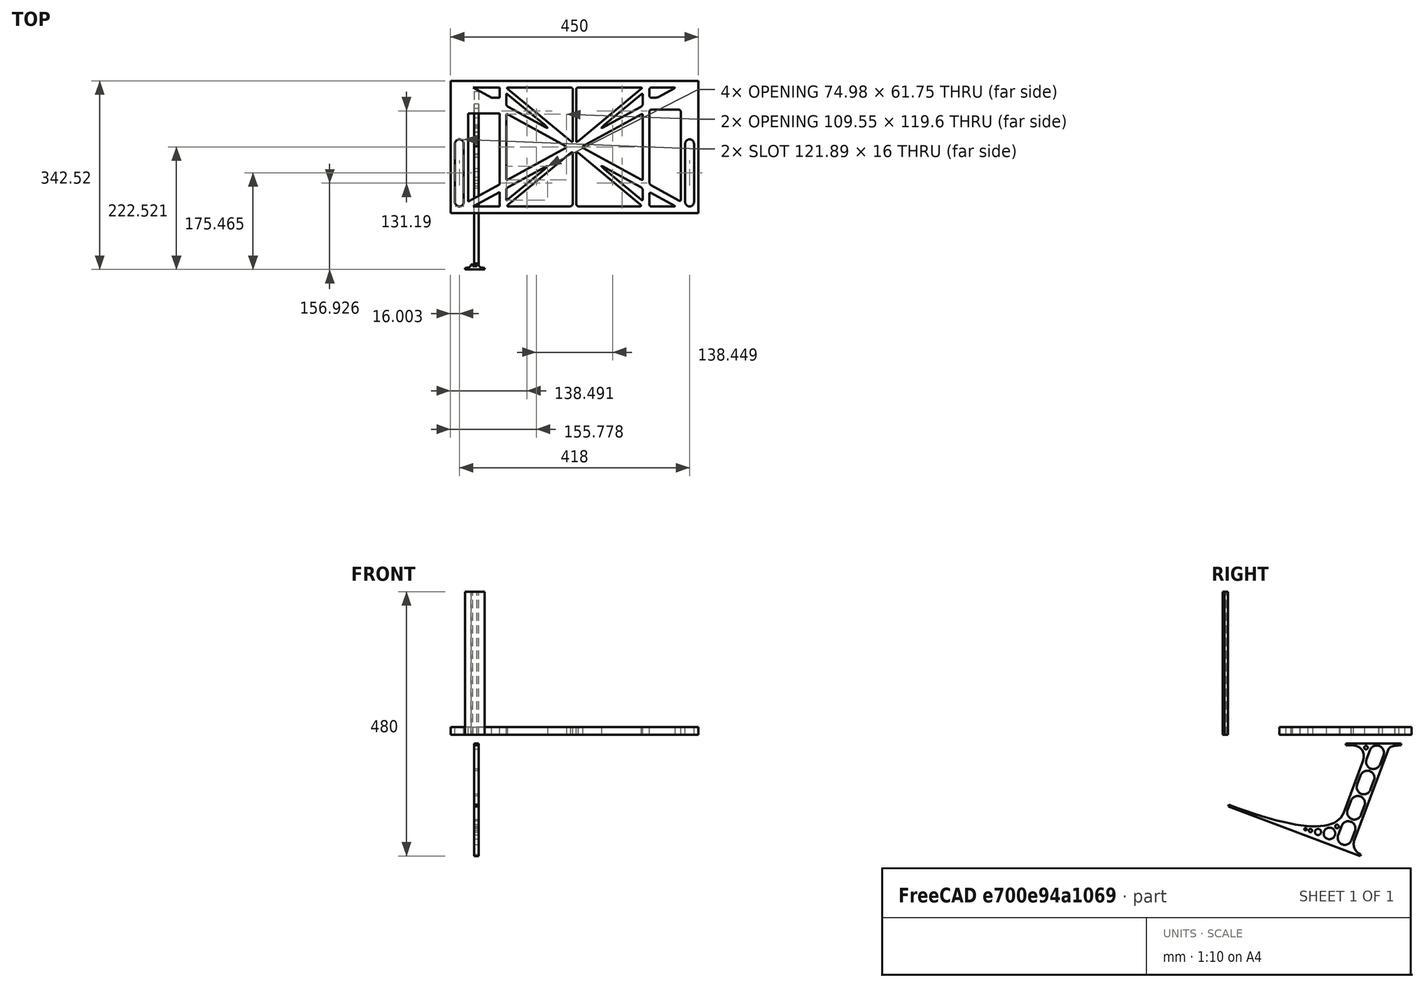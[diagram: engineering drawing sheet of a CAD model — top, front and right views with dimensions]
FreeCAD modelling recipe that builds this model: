
FCSTD DOCUMENT  (FreeCAD 0.19R0.19.2)
Label: laptopStand1145FCStd
License: All rights reserved
LicenseURL: http://en.wikipedia.org/wiki/All_rights_reserved
objects: Sketcher::SketchObject×3, Part::Extrusion×3
note: 6 computed .brp shape members not serialized (recipe doc carries the construction recipe); baked Part::Feature solids carry a one-line shape summary decoded from their .brp

FEATURE [Sketcher::SketchObject] Sketch
  FullyConstrained = false
  sketch-geometry (318):
    g0: LineSegment StartX=-10.9272 StartY=-82.7794 StartZ=0 EndX=46.0728 EndY=-51.4823 EndZ=0
    g1: LineSegment StartX=-10.9272 StartY=77.3346 StartZ=0 EndX=-10.9272 EndY=-82.7794 EndZ=0
    g2: LineSegment StartX=-1.92719 StartY=-91.7794 StartZ=0 EndX=46.0728 EndY=-91.7794 EndZ=0
    g3: LineSegment StartX=46.0728 StartY=-65.424 StartZ=0 EndX=-1.92719 EndY=-91.7794 EndZ=0
    g4: LineSegment StartX=46.0728 StartY=-65.424 StartZ=0 EndX=46.0728 EndY=-91.7794 EndZ=0
    g5: LineSegment StartX=46.0728 StartY=77.3346 StartZ=0 EndX=46.0728 EndY=-51.4823 EndZ=0
    g6: LineSegment StartX=-42.9272 StartY=136.221 StartZ=0 EndX=-42.9272 EndY=-103.779 EndZ=0
    g7: LineSegment StartX=407.073 StartY=136.221 StartZ=0 EndX=407.073 EndY=-103.779 EndZ=0
    g8: ArcOfCircle CenterX=-26.9272 CenterY=22.1087 CenterZ=0 NormalX=0 NormalY=0 NormalZ=1 AngleXU=0 Radius=8 StartAngle=1e-16 EndAngle=3.14159
    g9: ArcOfCircle CenterX=-26.9272 CenterY=-83.7794 CenterZ=0 NormalX=0 NormalY=0 NormalZ=1 AngleXU=0 Radius=8 StartAngle=3.14159 EndAngle=6.28319
    g10: LineSegment StartX=-34.9272 StartY=22.1087 StartZ=0 EndX=-34.9272 EndY=-83.7794 EndZ=0
    g11: LineSegment StartX=-18.9272 StartY=22.1087 StartZ=0 EndX=-18.9272 EndY=-83.7794 EndZ=0
    g12: ArcOfCircle CenterX=391.073 CenterY=22.1087 CenterZ=0 NormalX=0 NormalY=0 NormalZ=1 AngleXU=0 Radius=8 StartAngle=-4.4e-15 EndAngle=3.14159
    g13: LineSegment StartX=399.073 StartY=22.1087 StartZ=0 EndX=399.073 EndY=-83.7794 EndZ=0
    g14: LineSegment StartX=383.073 StartY=22.1087 StartZ=0 EndX=383.073 EndY=-83.7794 EndZ=0
    g15: ArcOfCircle CenterX=391.073 CenterY=-83.7794 CenterZ=0 NormalX=0 NormalY=0 NormalZ=1 AngleXU=0 Radius=8 StartAngle=3.14159 EndAngle=6.28319
    g16: Circle CenterX=175.022 CenterY=27.0628 CenterZ=0 NormalX=0 NormalY=0 NormalZ=1 AngleXU=0 Radius=1
    g17: Circle CenterX=179.022 CenterY=24.8665 CenterZ=0 NormalX=0 NormalY=0 NormalZ=1 AngleXU=0 Radius=1
    g18: Circle CenterX=179.022 CenterY=27.0628 CenterZ=0 NormalX=0 NormalY=0 NormalZ=1 AngleXU=0 Radius=1
    g19: BSplineCurve PolesCount=3 KnotsCount=2 Degree=2 IsPeriodic=0
    g20: GeomPoint X=175.022 Y=27.0628 Z=0
    g21: GeomPoint X=179.022 Y=27.0628 Z=0
    g22: Circle CenterX=189.124 CenterY=27.0628 CenterZ=0 NormalX=0 NormalY=0 NormalZ=1 AngleXU=0 Radius=1
    g23: Circle CenterX=185.124 CenterY=24.8665 CenterZ=0 NormalX=0 NormalY=0 NormalZ=1 AngleXU=0 Radius=1
    g24: Circle CenterX=185.124 CenterY=27.0628 CenterZ=0 NormalX=0 NormalY=0 NormalZ=1 AngleXU=0 Radius=1
    g25: BSplineCurve PolesCount=3 KnotsCount=2 Degree=2 IsPeriodic=0
    g26: GeomPoint X=189.124 Y=27.0628 Z=0
    g27: GeomPoint X=185.124 Y=27.0628 Z=0
    g28: Circle CenterX=175.022 CenterY=5.37834 CenterZ=0 NormalX=0 NormalY=0 NormalZ=1 AngleXU=0 Radius=1
    g29: Circle CenterX=179.022 CenterY=7.57463 CenterZ=0 NormalX=0 NormalY=0 NormalZ=1 AngleXU=0 Radius=1
    g30: Circle CenterX=179.022 CenterY=5.34704 CenterZ=0 NormalX=0 NormalY=0 NormalZ=1 AngleXU=0 Radius=1
    g31: BSplineCurve PolesCount=3 KnotsCount=2 Degree=2 IsPeriodic=0
    g32: GeomPoint X=175.022 Y=5.37834 Z=0
    g33: GeomPoint X=179.022 Y=5.34704 Z=0
    g34: Circle CenterX=189.124 CenterY=5.37834 CenterZ=0 NormalX=0 NormalY=0 NormalZ=1 AngleXU=0 Radius=1
    g35: Circle CenterX=185.124 CenterY=7.57463 CenterZ=0 NormalX=0 NormalY=0 NormalZ=1 AngleXU=0 Radius=1
    g36: Circle CenterX=185.124 CenterY=5.34704 CenterZ=0 NormalX=0 NormalY=0 NormalZ=1 AngleXU=0 Radius=1
    g37: BSplineCurve PolesCount=3 KnotsCount=2 Degree=2 IsPeriodic=0
    g38: GeomPoint X=189.124 Y=5.37834 Z=0
    g39: GeomPoint X=185.124 Y=5.34704 Z=0
    g40: Circle CenterX=165.871 CenterY=18.1458 CenterZ=0 NormalX=0 NormalY=0 NormalZ=1 AngleXU=0 Radius=1
    g41: Circle CenterX=169.377 CenterY=16.2206 CenterZ=0 NormalX=0 NormalY=0 NormalZ=1 AngleXU=0 Radius=1
    g42: Circle CenterX=165.871 CenterY=14.2954 CenterZ=0 NormalX=0 NormalY=0 NormalZ=1 AngleXU=0 Radius=1
    g43: BSplineCurve PolesCount=3 KnotsCount=2 Degree=2 IsPeriodic=0
    g44: GeomPoint X=165.871 Y=18.1458 Z=0
    g45: GeomPoint X=165.871 Y=14.2954 Z=0
    g46: Circle CenterX=198.275 CenterY=18.1458 CenterZ=0 NormalX=0 NormalY=0 NormalZ=1 AngleXU=0 Radius=1
    g47: Circle CenterX=194.768 CenterY=16.2206 CenterZ=0 NormalX=0 NormalY=0 NormalZ=1 AngleXU=0 Radius=1
    g48: Circle CenterX=198.275 CenterY=14.2954 CenterZ=0 NormalX=0 NormalY=0 NormalZ=1 AngleXU=0 Radius=1
    g49: BSplineCurve PolesCount=3 KnotsCount=2 Degree=2 IsPeriodic=0
    g50: GeomPoint X=198.275 Y=18.1458 Z=0
    g51: GeomPoint X=198.275 Y=14.2954 Z=0
    g52: LineSegment StartX=407.073 StartY=-103.779 StartZ=0 EndX=-42.9272 EndY=-103.779 EndZ=0
    g53: LineSegment StartX=407.073 StartY=136.221 StartZ=0 EndX=-42.9272 EndY=136.221 EndZ=0
    g54: LineSegment StartX=46.0728 StartY=77.3346 StartZ=0 EndX=-10.9272 EndY=77.3346 EndZ=0
    g55: LineSegment StartX=46.0728 StartY=105.865 StartZ=0 EndX=31.5028 EndY=105.865 EndZ=0
    g56: LineSegment StartX=46.0728 StartY=124.221 StartZ=0 EndX=46.0728 EndY=105.865 EndZ=0
    g57: LineSegment StartX=-1.92719 StartY=124.221 StartZ=0 EndX=31.5028 EndY=105.865 EndZ=0
    g58: LineSegment StartX=46.0728 StartY=124.221 StartZ=0 EndX=-1.92719 EndY=124.221 EndZ=0
    g59: Circle CenterX=125.607 CenterY=54.1951 CenterZ=0 NormalX=0 NormalY=0 NormalZ=1 AngleXU=0 Radius=1
    g60: Circle CenterX=139.632 CenterY=46.4944 CenterZ=0 NormalX=0 NormalY=0 NormalZ=1 AngleXU=0 Radius=1
    g61: Circle CenterX=127.326 CenterY=56.7187 CenterZ=0 NormalX=0 NormalY=0 NormalZ=1 AngleXU=0 Radius=1
    g62: BSplineCurve PolesCount=3 KnotsCount=2 Degree=2 IsPeriodic=0
    g63: GeomPoint X=125.607 Y=54.1951 Z=0
    g64: GeomPoint X=127.326 Y=56.7187 Z=0
    g65: Circle CenterX=236.821 CenterY=56.7187 CenterZ=0 NormalX=0 NormalY=0 NormalZ=1 AngleXU=0 Radius=1
    g66: Circle CenterX=224.513 CenterY=46.4944 CenterZ=0 NormalX=0 NormalY=0 NormalZ=1 AngleXU=0 Radius=1
    g67: Circle CenterX=238.538 CenterY=54.1951 CenterZ=0 NormalX=0 NormalY=0 NormalZ=1 AngleXU=0 Radius=1
    g68: BSplineCurve PolesCount=3 KnotsCount=2 Degree=2 IsPeriodic=0
    g69: GeomPoint X=236.821 Y=56.7187 Z=0
    g70: GeomPoint X=238.538 Y=54.1951 Z=0
    g71: Circle CenterX=238.538 CenterY=-21.7539 CenterZ=0 NormalX=0 NormalY=0 NormalZ=1 AngleXU=0 Radius=1
    g72: Circle CenterX=224.513 CenterY=-14.0532 CenterZ=0 NormalX=0 NormalY=0 NormalZ=1 AngleXU=0 Radius=1
    g73: Circle CenterX=236.821 CenterY=-24.2775 CenterZ=0 NormalX=0 NormalY=0 NormalZ=1 AngleXU=0 Radius=1
    g74: BSplineCurve PolesCount=3 KnotsCount=2 Degree=2 IsPeriodic=0
    g75: GeomPoint X=238.538 Y=-21.7539 Z=0
    g76: GeomPoint X=236.821 Y=-24.2775 Z=0
    g77: Circle CenterX=125.607 CenterY=-21.7539 CenterZ=0 NormalX=0 NormalY=0 NormalZ=1 AngleXU=0 Radius=1
    g78: Circle CenterX=139.632 CenterY=-14.0532 CenterZ=0 NormalX=0 NormalY=0 NormalZ=1 AngleXU=0 Radius=1
    g79: Circle CenterX=127.325 CenterY=-24.2775 CenterZ=0 NormalX=0 NormalY=0 NormalZ=1 AngleXU=0 Radius=1
    g80: BSplineCurve PolesCount=3 KnotsCount=2 Degree=2 IsPeriodic=0
    g81: GeomPoint X=125.607 Y=-21.7539 Z=0
    g82: GeomPoint X=127.325 Y=-24.2775 Z=0
    g83: Circle CenterX=302.996 CenterY=111.695 CenterZ=0 NormalX=0 NormalY=0 NormalZ=1 AngleXU=0 Radius=1
    g84: Circle CenterX=306.073 CenterY=114.251 CenterZ=0 NormalX=0 NormalY=0 NormalZ=1 AngleXU=0 Radius=1
    g85: Circle CenterX=306.073 CenterY=110.251 CenterZ=0 NormalX=0 NormalY=0 NormalZ=1 AngleXU=0 Radius=1
    g86: BSplineCurve PolesCount=3 KnotsCount=2 Degree=2 IsPeriodic=0
    g87: GeomPoint X=302.996 Y=111.695 Z=0
    g88: GeomPoint X=306.073 Y=110.251 Z=0
    g89: Circle CenterX=306.073 CenterY=95.2763 CenterZ=0 NormalX=0 NormalY=0 NormalZ=1 AngleXU=0 Radius=1
    g90: Circle CenterX=306.073 CenterY=91.2763 CenterZ=0 NormalX=0 NormalY=0 NormalZ=1 AngleXU=0 Radius=1
    g91: Circle CenterX=302.567 CenterY=89.3511 CenterZ=0 NormalX=0 NormalY=0 NormalZ=1 AngleXU=0 Radius=1
    g92: BSplineCurve PolesCount=3 KnotsCount=2 Degree=2 IsPeriodic=0
    g93: GeomPoint X=306.073 Y=95.2763 Z=0
    g94: GeomPoint X=302.567 Y=89.3511 Z=0
    g95: LineSegment StartX=306.073 StartY=110.251 StartZ=0 EndX=306.073 EndY=95.2763 EndZ=0
    g96: LineSegment StartX=302.996 StartY=111.695 StartZ=0 EndX=236.821 EndY=56.7187 EndZ=0
    g97: LineSegment StartX=238.538 StartY=54.1951 StartZ=0 EndX=302.567 EndY=89.3511 EndZ=0
    g98: Circle CenterX=61.1496 CenterY=111.695 CenterZ=0 NormalX=0 NormalY=0 NormalZ=1 AngleXU=0 Radius=1
    g99: Circle CenterX=58.0728 CenterY=114.251 CenterZ=0 NormalX=0 NormalY=0 NormalZ=1 AngleXU=0 Radius=1
    g100: Circle CenterX=58.0728 CenterY=110.251 CenterZ=0 NormalX=0 NormalY=0 NormalZ=1 AngleXU=0 Radius=1
    g101: BSplineCurve PolesCount=3 KnotsCount=2 Degree=2 IsPeriodic=0
    g102: GeomPoint X=61.1496 Y=111.695 Z=0
    g103: GeomPoint X=58.0728 Y=110.251 Z=0
    g104: Circle CenterX=61.5791 CenterY=89.3511 CenterZ=0 NormalX=0 NormalY=0 NormalZ=1 AngleXU=0 Radius=1
    g105: Circle CenterX=58.0728 CenterY=91.2763 CenterZ=0 NormalX=0 NormalY=0 NormalZ=1 AngleXU=0 Radius=1
    g106: Circle CenterX=58.0728 CenterY=95.2763 CenterZ=0 NormalX=0 NormalY=0 NormalZ=1 AngleXU=0 Radius=1
    g107: BSplineCurve PolesCount=3 KnotsCount=2 Degree=2 IsPeriodic=0
    g108: GeomPoint X=61.5791 Y=89.3511 Z=0
    g109: GeomPoint X=58.0728 Y=95.2763 Z=0
    g110: LineSegment StartX=58.0728 StartY=110.251 StartZ=0 EndX=58.0728 EndY=95.2763 EndZ=0
    g111: LineSegment StartX=61.1496 StartY=111.695 StartZ=0 EndX=127.326 EndY=56.7187 EndZ=0
    g112: LineSegment StartX=125.607 StartY=54.1951 StartZ=0 EndX=61.5791 EndY=89.3511 EndZ=0
    g113: Circle CenterX=61.5791 CenterY=-56.9099 CenterZ=0 NormalX=0 NormalY=0 NormalZ=1 AngleXU=0 Radius=1
    g114: Circle CenterX=58.0728 CenterY=-58.8351 CenterZ=0 NormalX=0 NormalY=0 NormalZ=1 AngleXU=0 Radius=1
    g115: Circle CenterX=58.0728 CenterY=-62.8351 CenterZ=0 NormalX=0 NormalY=0 NormalZ=1 AngleXU=0 Radius=1
    g116: BSplineCurve PolesCount=3 KnotsCount=2 Degree=2 IsPeriodic=0
    g117: GeomPoint X=61.5791 Y=-56.9099 Z=0
    g118: GeomPoint X=58.0728 Y=-62.8351 Z=0
    g119: Circle CenterX=58.0728 CenterY=-77.8102 CenterZ=0 NormalX=0 NormalY=0 NormalZ=1 AngleXU=0 Radius=1
    g120: Circle CenterX=58.0728 CenterY=-81.8102 CenterZ=0 NormalX=0 NormalY=0 NormalZ=1 AngleXU=0 Radius=1
    g121: Circle CenterX=61.1496 CenterY=-79.2541 CenterZ=0 NormalX=0 NormalY=0 NormalZ=1 AngleXU=0 Radius=1
    g122: BSplineCurve PolesCount=3 KnotsCount=2 Degree=2 IsPeriodic=0
    g123: GeomPoint X=58.0728 Y=-77.8102 Z=0
    g124: GeomPoint X=61.1496 Y=-79.2541 Z=0
    g125: LineSegment StartX=58.0728 StartY=-62.8351 StartZ=0 EndX=58.0728 EndY=-77.8102 EndZ=0
    g126: LineSegment StartX=61.1496 StartY=-79.2541 StartZ=0 EndX=127.325 EndY=-24.2775 EndZ=0
    g127: LineSegment StartX=125.607 StartY=-21.7539 StartZ=0 EndX=61.5791 EndY=-56.9099 EndZ=0
    g128: Circle CenterX=302.567 CenterY=-56.9099 CenterZ=0 NormalX=0 NormalY=0 NormalZ=1 AngleXU=0 Radius=1
    g129: Circle CenterX=306.073 CenterY=-58.8351 CenterZ=0 NormalX=0 NormalY=0 NormalZ=1 AngleXU=0 Radius=1
    g130: Circle CenterX=306.073 CenterY=-62.8351 CenterZ=0 NormalX=0 NormalY=0 NormalZ=1 AngleXU=0 Radius=1
    g131: BSplineCurve PolesCount=3 KnotsCount=2 Degree=2 IsPeriodic=0
    g132: GeomPoint X=302.567 Y=-56.9099 Z=0
    g133: GeomPoint X=306.073 Y=-62.8351 Z=0
    g134: Circle CenterX=302.996 CenterY=-79.2541 CenterZ=0 NormalX=0 NormalY=0 NormalZ=1 AngleXU=0 Radius=1
    g135: Circle CenterX=306.073 CenterY=-81.8102 CenterZ=0 NormalX=0 NormalY=0 NormalZ=1 AngleXU=0 Radius=1
    g136: Circle CenterX=306.073 CenterY=-77.8102 CenterZ=0 NormalX=0 NormalY=0 NormalZ=1 AngleXU=0 Radius=1
    g137: BSplineCurve PolesCount=3 KnotsCount=2 Degree=2 IsPeriodic=0
    g138: GeomPoint X=302.996 Y=-79.2541 Z=0
    g139: GeomPoint X=306.073 Y=-77.8102 Z=0
    g140: LineSegment StartX=306.073 StartY=-62.8351 StartZ=0 EndX=306.073 EndY=-77.8102 EndZ=0
    g141: LineSegment StartX=302.996 StartY=-79.2541 StartZ=0 EndX=236.821 EndY=-24.2775 EndZ=0
    g142: LineSegment StartX=238.538 StartY=-21.7539 StartZ=0 EndX=302.567 EndY=-56.9099 EndZ=0
    g143: Circle CenterX=61.6457 CenterY=-88.8112 CenterZ=0 NormalX=0 NormalY=0 NormalZ=1 AngleXU=0 Radius=1
    g144: Circle CenterX=58.0728 CenterY=-91.7794 CenterZ=0 NormalX=0 NormalY=0 NormalZ=1 AngleXU=0 Radius=1
    g145: Circle CenterX=63.9135 CenterY=-91.7794 CenterZ=0 NormalX=0 NormalY=0 NormalZ=1 AngleXU=0 Radius=1
    g146: BSplineCurve PolesCount=3 KnotsCount=2 Degree=2 IsPeriodic=0
    g147: GeomPoint X=61.6457 Y=-88.8112 Z=0
    g148: GeomPoint X=63.9135 Y=-91.7794 Z=0
    g149: Circle CenterX=179.022 CenterY=-85.8163 CenterZ=0 NormalX=0 NormalY=0 NormalZ=1 AngleXU=0 Radius=1
    g150: Circle CenterX=179.022 CenterY=-91.7794 CenterZ=0 NormalX=0 NormalY=0 NormalZ=1 AngleXU=0 Radius=1
    g151: Circle CenterX=171.895 CenterY=-91.7794 CenterZ=0 NormalX=0 NormalY=0 NormalZ=1 AngleXU=0 Radius=1
    g152: BSplineCurve PolesCount=3 KnotsCount=2 Degree=2 IsPeriodic=0
    g153: GeomPoint X=179.022 Y=-85.8163 Z=0
    g154: GeomPoint X=171.895 Y=-91.7794 Z=0
    g155: Circle CenterX=185.124 CenterY=-86.2028 CenterZ=0 NormalX=0 NormalY=0 NormalZ=1 AngleXU=0 Radius=1
    g156: Circle CenterX=185.124 CenterY=-91.7794 CenterZ=0 NormalX=0 NormalY=0 NormalZ=1 AngleXU=0 Radius=1
    g157: Circle CenterX=191.747 CenterY=-91.7794 CenterZ=0 NormalX=0 NormalY=0 NormalZ=1 AngleXU=0 Radius=1
    g158: BSplineCurve PolesCount=3 KnotsCount=2 Degree=2 IsPeriodic=0
    g159: GeomPoint X=185.124 Y=-86.2028 Z=0
    g160: GeomPoint X=191.747 Y=-91.7794 Z=0
    g161: Circle CenterX=299.888 CenterY=-86.6413 CenterZ=0 NormalX=0 NormalY=0 NormalZ=1 AngleXU=0 Radius=1
    g162: Circle CenterX=306.073 CenterY=-91.7794 CenterZ=0 NormalX=0 NormalY=0 NormalZ=1 AngleXU=0 Radius=1
    g163: Circle CenterX=298.776 CenterY=-91.7794 CenterZ=0 NormalX=0 NormalY=0 NormalZ=1 AngleXU=0 Radius=1
    g164: BSplineCurve PolesCount=3 KnotsCount=2 Degree=2 IsPeriodic=0
    g165: GeomPoint X=299.888 Y=-86.6413 Z=0
    g166: GeomPoint X=298.776 Y=-91.7794 Z=0
    g167: LineSegment StartX=189.124 StartY=5.37834 StartZ=0 EndX=299.888 EndY=-86.6413 EndZ=0
    g168: LineSegment StartX=298.776 StartY=-91.7794 StartZ=0 EndX=191.747 EndY=-91.7794 EndZ=0
    g169: LineSegment StartX=185.124 StartY=-86.2028 StartZ=0 EndX=185.124 EndY=5.34704 EndZ=0
    g170: LineSegment StartX=179.022 StartY=5.34704 StartZ=0 EndX=179.022 EndY=-85.8163 EndZ=0
    g171: LineSegment StartX=171.895 StartY=-91.7794 StartZ=0 EndX=63.9135 EndY=-91.7794 EndZ=0
    g172: LineSegment StartX=61.6457 StartY=-88.8112 StartZ=0 EndX=175.022 EndY=5.37834 EndZ=0
    g173: Circle CenterX=302.073 CenterY=124.221 CenterZ=0 NormalX=0 NormalY=0 NormalZ=1 AngleXU=0 Radius=1
    g174: Circle CenterX=306.073 CenterY=124.221 CenterZ=0 NormalX=0 NormalY=0 NormalZ=1 AngleXU=0 Radius=1
    g175: Circle CenterX=302.996 CenterY=121.665 CenterZ=0 NormalX=0 NormalY=0 NormalZ=1 AngleXU=0 Radius=1
    g176: BSplineCurve PolesCount=3 KnotsCount=2 Degree=2 IsPeriodic=0
    g177: GeomPoint X=302.073 Y=124.221 Z=0
    g178: GeomPoint X=302.996 Y=121.665 Z=0
    g179: Circle CenterX=189.124 CenterY=124.221 CenterZ=0 NormalX=0 NormalY=0 NormalZ=1 AngleXU=0 Radius=1
    g180: Circle CenterX=185.124 CenterY=124.221 CenterZ=0 NormalX=0 NormalY=0 NormalZ=1 AngleXU=0 Radius=1
    g181: Circle CenterX=185.124 CenterY=120.221 CenterZ=0 NormalX=0 NormalY=0 NormalZ=1 AngleXU=0 Radius=1
    g182: BSplineCurve PolesCount=3 KnotsCount=2 Degree=2 IsPeriodic=0
    g183: GeomPoint X=189.124 Y=124.221 Z=0
    g184: GeomPoint X=185.124 Y=120.221 Z=0
    g185: Circle CenterX=175.022 CenterY=124.221 CenterZ=0 NormalX=0 NormalY=0 NormalZ=1 AngleXU=0 Radius=1
    g186: Circle CenterX=179.022 CenterY=124.221 CenterZ=0 NormalX=0 NormalY=0 NormalZ=1 AngleXU=0 Radius=1
    g187: Circle CenterX=179.022 CenterY=120.221 CenterZ=0 NormalX=0 NormalY=0 NormalZ=1 AngleXU=0 Radius=1
    g188: BSplineCurve PolesCount=3 KnotsCount=2 Degree=2 IsPeriodic=0
    g189: GeomPoint X=175.022 Y=124.221 Z=0
    g190: GeomPoint X=179.022 Y=120.221 Z=0
    g191: Circle CenterX=62.0728 CenterY=124.221 CenterZ=0 NormalX=0 NormalY=0 NormalZ=1 AngleXU=0 Radius=1
    g192: Circle CenterX=58.0728 CenterY=124.221 CenterZ=0 NormalX=0 NormalY=0 NormalZ=1 AngleXU=0 Radius=1
    g193: Circle CenterX=61.1496 CenterY=121.665 CenterZ=0 NormalX=0 NormalY=0 NormalZ=1 AngleXU=0 Radius=1
    g194: BSplineCurve PolesCount=3 KnotsCount=2 Degree=2 IsPeriodic=0
    g195: GeomPoint X=62.0728 Y=124.221 Z=0
    g196: GeomPoint X=61.1496 Y=121.665 Z=0
    g197: LineSegment StartX=62.0728 StartY=124.221 StartZ=0 EndX=175.022 EndY=124.221 EndZ=0
    g198: LineSegment StartX=179.022 StartY=120.221 StartZ=0 EndX=179.022 EndY=27.0628 EndZ=0
    g199: LineSegment StartX=185.124 StartY=27.0628 StartZ=0 EndX=185.124 EndY=120.221 EndZ=0
    g200: LineSegment StartX=189.124 StartY=124.221 StartZ=0 EndX=302.073 EndY=124.221 EndZ=0
    g201: LineSegment StartX=302.996 StartY=121.665 StartZ=0 EndX=189.124 EndY=27.0628 EndZ=0
    g202: LineSegment StartX=175.022 StartY=27.0628 StartZ=0 EndX=61.1496 EndY=121.665 EndZ=0
    g203: Circle CenterX=61.5791 CenterY=75.4095 CenterZ=0 NormalX=0 NormalY=0 NormalZ=1 AngleXU=0 Radius=1
    g204: Circle CenterX=58.0728 CenterY=77.3346 CenterZ=0 NormalX=0 NormalY=0 NormalZ=1 AngleXU=0 Radius=1
    g205: Circle CenterX=58.0728 CenterY=73.3346 CenterZ=0 NormalX=0 NormalY=0 NormalZ=1 AngleXU=0 Radius=1
    g206: BSplineCurve PolesCount=3 KnotsCount=2 Degree=2 IsPeriodic=0
    g207: GeomPoint X=61.5791 Y=75.4095 Z=0
    g208: GeomPoint X=58.0728 Y=73.3346 Z=0
    g209: Circle CenterX=58.0728 CenterY=-40.8935 CenterZ=0 NormalX=0 NormalY=0 NormalZ=1 AngleXU=0 Radius=1
    g210: Circle CenterX=58.0728 CenterY=-44.8935 CenterZ=0 NormalX=0 NormalY=0 NormalZ=1 AngleXU=0 Radius=1
    g211: Circle CenterX=61.5791 CenterY=-42.9683 CenterZ=0 NormalX=0 NormalY=0 NormalZ=1 AngleXU=0 Radius=1
    g212: BSplineCurve PolesCount=3 KnotsCount=2 Degree=2 IsPeriodic=0
    g213: GeomPoint X=58.0728 Y=-40.8935 Z=0
    g214: GeomPoint X=61.5791 Y=-42.9683 Z=0
    g215: LineSegment StartX=61.5791 StartY=-42.9683 StartZ=0 EndX=165.871 EndY=14.2954 EndZ=0
    g216: LineSegment StartX=165.871 StartY=18.1458 StartZ=0 EndX=61.5791 EndY=75.4095 EndZ=0
    g217: LineSegment StartX=58.0728 StartY=73.3346 StartZ=0 EndX=58.0728 EndY=-40.8935 EndZ=0
    g218: Circle CenterX=302.567 CenterY=-42.9683 CenterZ=0 NormalX=0 NormalY=0 NormalZ=1 AngleXU=0 Radius=1
    g219: Circle CenterX=306.073 CenterY=-44.8935 CenterZ=0 NormalX=0 NormalY=0 NormalZ=1 AngleXU=0 Radius=1
    g220: Circle CenterX=306.073 CenterY=-40.8935 CenterZ=0 NormalX=0 NormalY=0 NormalZ=1 AngleXU=0 Radius=1
    g221: BSplineCurve PolesCount=3 KnotsCount=2 Degree=2 IsPeriodic=0
    g222: GeomPoint X=302.567 Y=-42.9683 Z=0
    g223: GeomPoint X=306.073 Y=-40.8935 Z=0
    g224: Circle CenterX=306.073 CenterY=73.3346 CenterZ=0 NormalX=0 NormalY=0 NormalZ=1 AngleXU=0 Radius=1
    g225: Circle CenterX=306.073 CenterY=77.3346 CenterZ=0 NormalX=0 NormalY=0 NormalZ=1 AngleXU=0 Radius=1
    g226: Circle CenterX=302.567 CenterY=75.4095 CenterZ=0 NormalX=0 NormalY=0 NormalZ=1 AngleXU=0 Radius=1
    g227: BSplineCurve PolesCount=3 KnotsCount=2 Degree=2 IsPeriodic=0
    g228: GeomPoint X=306.073 Y=73.3346 Z=0
    g229: GeomPoint X=302.567 Y=75.4095 Z=0
    g230: LineSegment StartX=302.567 StartY=-42.9683 StartZ=0 EndX=198.275 EndY=14.2954 EndZ=0
    g231: LineSegment StartX=198.275 StartY=18.1458 StartZ=0 EndX=302.567 EndY=75.4095 EndZ=0
    g232: LineSegment StartX=306.073 StartY=73.3346 StartZ=0 EndX=306.073 EndY=-40.8935 EndZ=0
    g233: LineSegment StartX=322.073 StartY=105.865 StartZ=0 EndX=328.643 EndY=105.865 EndZ=0
    g234: LineSegment StartX=318.073 StartY=120.221 StartZ=0 EndX=318.073 EndY=109.865 EndZ=0
    g235: LineSegment StartX=336.157 StartY=107.779 StartZ=0 EndX=362.567 EndY=122.294 EndZ=0
    g236: Circle CenterX=362.073 CenterY=124.221 CenterZ=0 NormalX=0 NormalY=0 NormalZ=1 AngleXU=0 Radius=1
    g237: Circle CenterX=366.073 CenterY=124.221 CenterZ=0 NormalX=0 NormalY=0 NormalZ=1 AngleXU=0 Radius=1
    g238: Circle CenterX=362.567 CenterY=122.294 CenterZ=0 NormalX=0 NormalY=0 NormalZ=1 AngleXU=0 Radius=1
    g239: BSplineCurve PolesCount=3 KnotsCount=2 Degree=2 IsPeriodic=0
    g240: GeomPoint X=362.073 Y=124.221 Z=0
    g241: GeomPoint X=362.567 Y=122.294 Z=0
    g242: Circle CenterX=322.073 CenterY=124.221 CenterZ=0 NormalX=0 NormalY=0 NormalZ=1 AngleXU=0 Radius=1
    g243: Circle CenterX=318.073 CenterY=124.221 CenterZ=0 NormalX=0 NormalY=0 NormalZ=1 AngleXU=0 Radius=1
    g244: Circle CenterX=318.073 CenterY=120.221 CenterZ=0 NormalX=0 NormalY=0 NormalZ=1 AngleXU=0 Radius=1
    g245: BSplineCurve PolesCount=3 KnotsCount=2 Degree=2 IsPeriodic=0
    g246: GeomPoint X=322.073 Y=124.221 Z=0
    g247: GeomPoint X=318.073 Y=120.221 Z=0
    g248: Circle CenterX=322.073 CenterY=105.865 CenterZ=0 NormalX=0 NormalY=0 NormalZ=1 AngleXU=0 Radius=1
    g249: Circle CenterX=318.073 CenterY=105.865 CenterZ=0 NormalX=0 NormalY=0 NormalZ=1 AngleXU=0 Radius=1
    g250: Circle CenterX=318.073 CenterY=109.865 CenterZ=0 NormalX=0 NormalY=0 NormalZ=1 AngleXU=0 Radius=1
    g251: BSplineCurve PolesCount=3 KnotsCount=2 Degree=2 IsPeriodic=0
    g252: GeomPoint X=322.073 Y=105.865 Z=0
    g253: GeomPoint X=318.073 Y=109.865 Z=0
    g254: Circle CenterX=336.157 CenterY=107.779 CenterZ=0 NormalX=0 NormalY=0 NormalZ=1 AngleXU=0 Radius=1
    g255: Circle CenterX=332.651 CenterY=105.853 CenterZ=0 NormalX=0 NormalY=0 NormalZ=1 AngleXU=0 Radius=1
    g256: Circle CenterX=328.643 CenterY=105.865 CenterZ=0 NormalX=0 NormalY=0 NormalZ=1 AngleXU=0 Radius=1
    g257: BSplineCurve PolesCount=3 KnotsCount=2 Degree=2 IsPeriodic=0
    g258: GeomPoint X=336.157 Y=107.779 Z=0
    g259: GeomPoint X=328.643 Y=105.865 Z=0
    g260: LineSegment StartX=322.073 StartY=124.221 StartZ=0 EndX=362.073 EndY=124.221 EndZ=0
    g261: Circle CenterX=371.567 CenterY=-80.8644 CenterZ=0 NormalX=0 NormalY=0 NormalZ=1 AngleXU=0 Radius=1
    g262: Circle CenterX=375.073 CenterY=-82.7896 CenterZ=0 NormalX=0 NormalY=0 NormalZ=1 AngleXU=0 Radius=1
    g263: Circle CenterX=375.073 CenterY=-78.7896 CenterZ=0 NormalX=0 NormalY=0 NormalZ=1 AngleXU=0 Radius=1
    g264: BSplineCurve PolesCount=3 KnotsCount=2 Degree=2 IsPeriodic=0
    g265: GeomPoint X=371.567 Y=-80.8644 Z=0
    g266: GeomPoint X=375.073 Y=-78.7896 Z=0
    g267: Circle CenterX=321.579 CenterY=-53.4075 CenterZ=0 NormalX=0 NormalY=0 NormalZ=1 AngleXU=0 Radius=1
    g268: Circle CenterX=318.073 CenterY=-51.4823 CenterZ=0 NormalX=0 NormalY=0 NormalZ=1 AngleXU=0 Radius=1
    g269: Circle CenterX=318.073 CenterY=-47.4823 CenterZ=0 NormalX=0 NormalY=0 NormalZ=1 AngleXU=0 Radius=1
    g270: BSplineCurve PolesCount=3 KnotsCount=2 Degree=2 IsPeriodic=0
    g271: GeomPoint X=321.579 Y=-53.4075 Z=0
    g272: GeomPoint X=318.073 Y=-47.4823 Z=0
    g273: Circle CenterX=318.073 CenterY=79.9235 CenterZ=0 NormalX=0 NormalY=0 NormalZ=1 AngleXU=0 Radius=1
    g274: Circle CenterX=318.073 CenterY=83.9235 CenterZ=0 NormalX=0 NormalY=0 NormalZ=1 AngleXU=0 Radius=1
    g275: Circle CenterX=322.073 CenterY=83.9235 CenterZ=0 NormalX=0 NormalY=0 NormalZ=1 AngleXU=0 Radius=1
    g276: BSplineCurve PolesCount=3 KnotsCount=2 Degree=2 IsPeriodic=0
    g277: GeomPoint X=318.073 Y=79.9235 Z=0
    g278: GeomPoint X=322.073 Y=83.9235 Z=0
    g279: Circle CenterX=375.073 CenterY=79.9235 CenterZ=0 NormalX=0 NormalY=0 NormalZ=1 AngleXU=0 Radius=1
    g280: Circle CenterX=375.073 CenterY=83.9235 CenterZ=0 NormalX=0 NormalY=0 NormalZ=1 AngleXU=0 Radius=1
    g281: Circle CenterX=371.073 CenterY=83.9235 CenterZ=0 NormalX=0 NormalY=0 NormalZ=1 AngleXU=0 Radius=1
    g282: BSplineCurve PolesCount=3 KnotsCount=2 Degree=2 IsPeriodic=0
    g283: GeomPoint X=375.073 Y=79.9235 Z=0
    g284: GeomPoint X=371.073 Y=83.9235 Z=0
    g285: LineSegment StartX=322.073 StartY=83.9235 StartZ=0 EndX=371.073 EndY=83.9235 EndZ=0
    g286: LineSegment StartX=375.073 StartY=79.9235 StartZ=0 EndX=375.073 EndY=-78.7896 EndZ=0
    g287: LineSegment StartX=371.567 StartY=-80.8644 StartZ=0 EndX=321.579 EndY=-53.4075 EndZ=0
    g288: LineSegment StartX=318.073 StartY=-47.4823 StartZ=0 EndX=318.073 EndY=79.9235 EndZ=0
    g289: Circle CenterX=321.579 CenterY=-67.3492 CenterZ=0 NormalX=0 NormalY=0 NormalZ=1 AngleXU=0 Radius=1
    g290: Circle CenterX=318.073 CenterY=-65.424 CenterZ=0 NormalX=0 NormalY=0 NormalZ=1 AngleXU=0 Radius=1
    g291: Circle CenterX=318.073 CenterY=-69.424 CenterZ=0 NormalX=0 NormalY=0 NormalZ=1 AngleXU=0 Radius=1
    g292: BSplineCurve PolesCount=3 KnotsCount=2 Degree=2 IsPeriodic=0
    g293: GeomPoint X=321.579 Y=-67.3492 Z=0
    g294: GeomPoint X=318.073 Y=-69.424 Z=0
    g295: Circle CenterX=362.567 CenterY=-89.8542 CenterZ=0 NormalX=0 NormalY=0 NormalZ=1 AngleXU=0 Radius=1
    g296: Circle CenterX=366.073 CenterY=-91.7794 CenterZ=0 NormalX=0 NormalY=0 NormalZ=1 AngleXU=0 Radius=1
    g297: Circle CenterX=362.073 CenterY=-91.7794 CenterZ=0 NormalX=0 NormalY=0 NormalZ=1 AngleXU=0 Radius=1
    g298: BSplineCurve PolesCount=3 KnotsCount=2 Degree=2 IsPeriodic=0
    g299: GeomPoint X=362.567 Y=-89.8542 Z=0
    g300: GeomPoint X=362.073 Y=-91.7794 Z=0
    g301: Circle CenterX=322.073 CenterY=-91.7794 CenterZ=0 NormalX=0 NormalY=0 NormalZ=1 AngleXU=0 Radius=1
    g302: Circle CenterX=318.073 CenterY=-91.7794 CenterZ=0 NormalX=0 NormalY=0 NormalZ=1 AngleXU=0 Radius=1
    g303: Circle CenterX=318.073 CenterY=-87.7794 CenterZ=0 NormalX=0 NormalY=0 NormalZ=1 AngleXU=0 Radius=1
    g304: BSplineCurve PolesCount=3 KnotsCount=2 Degree=2 IsPeriodic=0
    g305: GeomPoint X=322.073 Y=-91.7794 Z=0
    g306: GeomPoint X=318.073 Y=-87.7794 Z=0
    g307: LineSegment StartX=362.567 StartY=-89.8542 StartZ=0 EndX=321.579 EndY=-67.3492 EndZ=0
    g308: LineSegment StartX=318.073 StartY=-69.424 StartZ=0 EndX=318.073 EndY=-87.7794 EndZ=0
    g309: LineSegment StartX=322.073 StartY=-91.7794 StartZ=0 EndX=362.073 EndY=-91.7794 EndZ=0
    g310: LineSegment StartX=-1.22313 StartY=125.592 StartZ=0 EndX=2.77687 EndY=125.592 EndZ=0
    g311: LineSegment StartX=-1.75029 StartY=122.959 StartZ=0 EndX=1.91164 EndY=121.35 EndZ=0
    g312: LineSegment StartX=30.6381 StartY=105.057 StartZ=0 EndX=27.0814 EndY=106.888 EndZ=0
    g313: LineSegment StartX=31.7735 StartY=104.735 StartZ=0 EndX=35.7735 EndY=104.735 EndZ=0
    g314: LineSegment StartX=46.1449 StartY=104.994 StartZ=0 EndX=42.1449 EndY=104.994 EndZ=0
    g315: LineSegment StartX=47.084 StartY=105.387 StartZ=0 EndX=47.084 EndY=109.387 EndZ=0
    g316: LineSegment StartX=47.1703 StartY=124.415 StartZ=0 EndX=47.1703 EndY=120.415 EndZ=0
    g317: LineSegment StartX=46.5031 StartY=125.161 StartZ=0 EndX=42.5031 EndY=125.161 EndZ=0
  constraints (533):
    c: Horizontal(g2)
    c: Coincident(g4,g3)
    c: Coincident(g0,g5)
    c: Block(g4)
    c: Block(g3)
    c: Block(g0)
    c: Block(g1)
    c: Block(g2)
    c: Vertical(g6)
    c: Vertical(g7)
    c: Block(g7)
    c: Block(g6)
    c: Tangent(g8,g11) = 1.5708
    c: Tangent(g8,g10) = -1.5708
    c: Tangent(g10,g9) = -1.5708
    c: Tangent(g11,g9) = 1.5708
    c: Vertical(g10)
    c: Equal(g8,g9)
    c: Block(g11)
    c: Block(g10)
    c: Tangent(g12,g13) = 1.5708
    c: Tangent(g13,g15) = 1.5708
    c: Equal(g12,g15)
    c: Coincident(g14,g12)
    c: Coincident(g14,g15)
    c: Block(g13)
    c: Block(g14)
    c: Weight(g16) = 1
    c: Equal(g16,g17)
    c: Equal(g16,g18)
    c: InternalAlignment(g16,g19)
    c: InternalAlignment(g17,g19)
    c: InternalAlignment(g18,g19)
    c: InternalAlignment(g20,g19)
    c: InternalAlignment(g21,g19)
    c: Weight(g22) = 1
    c: Equal(g22,g23)
    c: Equal(g22,g24)
    c: InternalAlignment(g22,g25)
    c: InternalAlignment(g23,g25)
    c: InternalAlignment(g24,g25)
    c: InternalAlignment(g26,g25)
    c: InternalAlignment(g27,g25)
    c: Block(g25)
    c: Block(g19)
    c: Weight(g28) = 1
    c: Equal(g28,g29)
    c: Equal(g28,g30)
    c: InternalAlignment(g28,g31)
    c: InternalAlignment(g29,g31)
    c: InternalAlignment(g30,g31)
    c: InternalAlignment(g32,g31)
    c: InternalAlignment(g33,g31)
    c: Weight(g34) = 1
    c: Equal(g34,g35)
    c: Equal(g34,g36)
    c: InternalAlignment(g34,g37)
    c: InternalAlignment(g35,g37)
    c: InternalAlignment(g36,g37)
    c: InternalAlignment(g38,g37)
    c: InternalAlignment(g39,g37)
    c: Block(g37)
    c: Block(g31)
    c: Weight(g40) = 1
    c: Equal(g40,g41)
    c: Equal(g40,g42)
    c: InternalAlignment(g40,g43)
    c: InternalAlignment(g41,g43)
    c: InternalAlignment(g42,g43)
    c: InternalAlignment(g44,g43)
    c: InternalAlignment(g45,g43)
    c: Weight(g46) = 1
    c: Equal(g46,g47)
    c: Equal(g46,g48)
    c: InternalAlignment(g46,g49)
    c: InternalAlignment(g47,g49)
    c: InternalAlignment(g48,g49)
    c: InternalAlignment(g50,g49)
    c: InternalAlignment(g51,g49)
    c: Block(g43)
    c: Block(g49)
    c: Coincident(g52,g7)
    c: Coincident(g52,g6)
    c: Horizontal(g52)
    c: Distance(g52) = 450
    c: Coincident(g53,g7)
    c: Coincident(g53,g6)
    c: Horizontal(g53)
    c: Horizontal(g54)
    c: Coincident(g5,g54)
    c: Horizontal(g55)
    c: Vertical(g56)
    c: Block(g56)
    c: Block(g55)
    c: Block(g54)
    c: Distance(g56) = 18.3554
    c: Coincident(g58,g56)
    c: Coincident(g58,g57)
    c: Horizontal(g58)
    c: Block(g58)
    c: Block(g57)
    c: Coincident(g55,g57)
    c: Coincident(g1,g54)
    c: Weight(g59) = 1
    c: Equal(g59,g60)
    c: Equal(g59,g61)
    c: InternalAlignment(g59,g62)
    c: InternalAlignment(g60,g62)
    c: InternalAlignment(g61,g62)
    c: InternalAlignment(g63,g62)
    c: InternalAlignment(g64,g62)
    c: Block(g62)
    c: Weight(g65) = 1
    c: Equal(g65,g66)
    c: Equal(g65,g67)
    c: InternalAlignment(g65,g68)
    c: InternalAlignment(g66,g68)
    c: InternalAlignment(g67,g68)
    c: InternalAlignment(g69,g68)
    c: InternalAlignment(g70,g68)
    c: Block(g68)
    c: Weight(g71) = 1
    c: Equal(g71,g72)
    c: Equal(g71,g73)
    c: InternalAlignment(g71,g74)
    c: InternalAlignment(g72,g74)
    c: InternalAlignment(g73,g74)
    c: InternalAlignment(g75,g74)
    c: InternalAlignment(g76,g74)
    c: Block(g74)
    c: Weight(g77) = 1
    c: Equal(g77,g78)
    c: Equal(g77,g79)
    c: InternalAlignment(g77,g80)
    c: InternalAlignment(g78,g80)
    c: InternalAlignment(g79,g80)
    c: InternalAlignment(g81,g80)
    c: InternalAlignment(g82,g80)
    c: Block(g80)
    c: Weight(g83) = 1
    c: Equal(g83,g84)
    c: Equal(g83,g85)
    c: InternalAlignment(g83,g86)
    c: InternalAlignment(g84,g86)
    c: InternalAlignment(g85,g86)
    c: InternalAlignment(g87,g86)
    c: InternalAlignment(g88,g86)
    c: Weight(g89) = 1
    c: Equal(g89,g90)
    c: Equal(g89,g91)
    c: InternalAlignment(g89,g92)
    c: InternalAlignment(g90,g92)
    c: InternalAlignment(g91,g92)
    c: InternalAlignment(g93,g92)
    c: InternalAlignment(g94,g92)
    c: Block(g86)
    c: Block(g92)
    c: Coincident(g95,g86)
    c: Coincident(g95,g92)
    c: Vertical(g95)
    c: Coincident(g96,g86)
    c: Coincident(g96,g68)
    c: Coincident(g97,g68)
    c: Coincident(g97,g92)
    c: Weight(g98) = 1
    c: Equal(g98,g99)
    c: Equal(g98,g100)
    c: InternalAlignment(g98,g101)
    c: InternalAlignment(g99,g101)
    c: InternalAlignment(g100,g101)
    c: InternalAlignment(g102,g101)
    c: InternalAlignment(g103,g101)
    c: Weight(g104) = 1
    c: Equal(g104,g105)
    c: Equal(g104,g106)
    c: InternalAlignment(g104,g107)
    c: InternalAlignment(g105,g107)
    c: InternalAlignment(g106,g107)
    c: InternalAlignment(g108,g107)
    c: InternalAlignment(g109,g107)
    c: Block(g101)
    c: Block(g107)
    c: Coincident(g110,g101)
    c: Coincident(g110,g107)
    c: Vertical(g110)
    c: Coincident(g111,g101)
    c: Coincident(g111,g62)
    c: Coincident(g112,g62)
    c: Coincident(g112,g107)
    c: Weight(g113) = 1
    c: Equal(g113,g114)
    c: Equal(g113,g115)
    c: InternalAlignment(g113,g116)
    c: InternalAlignment(g114,g116)
    c: InternalAlignment(g115,g116)
    c: InternalAlignment(g117,g116)
    c: InternalAlignment(g118,g116)
    c: Weight(g119) = 1
    c: Equal(g119,g120)
    c: Equal(g119,g121)
    c: InternalAlignment(g119,g122)
    c: InternalAlignment(g120,g122)
    c: InternalAlignment(g121,g122)
    c: InternalAlignment(g123,g122)
    c: InternalAlignment(g124,g122)
    c: Block(g116)
    c: Block(g122)
    c: Coincident(g125,g116)
    c: Coincident(g125,g122)
    c: Vertical(g125)
    c: Coincident(g126,g122)
    c: Coincident(g126,g80)
    c: Coincident(g127,g80)
    c: Coincident(g127,g116)
    c: Weight(g128) = 1
    c: Equal(g128,g129)
    c: Equal(g128,g130)
    c: InternalAlignment(g128,g131)
    c: InternalAlignment(g129,g131)
    c: InternalAlignment(g130,g131)
    c: InternalAlignment(g132,g131)
    c: InternalAlignment(g133,g131)
    c: Weight(g134) = 1
    c: Equal(g134,g135)
    c: Equal(g134,g136)
    c: InternalAlignment(g134,g137)
    c: InternalAlignment(g135,g137)
    c: InternalAlignment(g136,g137)
    c: InternalAlignment(g138,g137)
    c: InternalAlignment(g139,g137)
    c: Block(g131)
    c: Block(g137)
    c: Coincident(g140,g131)
    c: Coincident(g140,g137)
    c: Vertical(g140)
    c: Coincident(g141,g137)
    c: Coincident(g141,g74)
    c: Coincident(g142,g74)
    c: Coincident(g142,g131)
    c: Weight(g143) = 1
    c: Equal(g143,g144)
    c: Equal(g143,g145)
    c: InternalAlignment(g143,g146)
    c: InternalAlignment(g144,g146)
    c: InternalAlignment(g145,g146)
    c: InternalAlignment(g147,g146)
    c: InternalAlignment(g148,g146)
    c: Weight(g149) = 1
    c: Equal(g149,g150)
    c: Equal(g149,g151)
    c: InternalAlignment(g149,g152)
    c: InternalAlignment(g150,g152)
    c: InternalAlignment(g151,g152)
    c: InternalAlignment(g153,g152)
    c: InternalAlignment(g154,g152)
    c: Weight(g155) = 1
    c: Equal(g155,g156)
    c: Equal(g155,g157)
    c: InternalAlignment(g155,g158)
    c: InternalAlignment(g156,g158)
    c: InternalAlignment(g157,g158)
    c: InternalAlignment(g159,g158)
    c: InternalAlignment(g160,g158)
    c: Weight(g161) = 1
    c: Equal(g161,g162)
    c: Equal(g161,g163)
    c: InternalAlignment(g161,g164)
    c: InternalAlignment(g162,g164)
    c: InternalAlignment(g163,g164)
    c: InternalAlignment(g165,g164)
    c: InternalAlignment(g166,g164)
    c: Block(g164)
    c: Block(g158)
    c: Block(g152)
    c: Block(g146)
    c: Coincident(g167,g37)
    c: Coincident(g167,g164)
    c: Coincident(g168,g164)
    c: Coincident(g168,g158)
    c: Horizontal(g168)
    c: Coincident(g169,g158)
    c: Coincident(g169,g37)
    c: Vertical(g169)
    c: Coincident(g170,g31)
    c: Coincident(g170,g152)
    c: Vertical(g170)
    c: Coincident(g171,g152)
    c: Coincident(g171,g146)
    c: Horizontal(g171)
    c: Coincident(g172,g146)
    c: Coincident(g172,g31)
    c: Weight(g173) = 1
    c: Equal(g173,g174)
    c: Equal(g173,g175)
    c: InternalAlignment(g173,g176)
    c: InternalAlignment(g174,g176)
    c: InternalAlignment(g175,g176)
    c: InternalAlignment(g177,g176)
    c: InternalAlignment(g178,g176)
    c: Weight(g179) = 1
    c: Equal(g179,g180)
    c: Equal(g179,g181)
    c: InternalAlignment(g179,g182)
    c: InternalAlignment(g180,g182)
    c: InternalAlignment(g181,g182)
    c: InternalAlignment(g183,g182)
    c: InternalAlignment(g184,g182)
    c: Weight(g185) = 1
    c: Equal(g185,g186)
    c: Equal(g185,g187)
    c: InternalAlignment(g185,g188)
    c: InternalAlignment(g186,g188)
    c: InternalAlignment(g187,g188)
    c: InternalAlignment(g189,g188)
    c: InternalAlignment(g190,g188)
    c: Weight(g191) = 1
    c: Equal(g191,g192)
    c: Equal(g191,g193)
    c: InternalAlignment(g191,g194)
    c: InternalAlignment(g192,g194)
    c: InternalAlignment(g193,g194)
    c: InternalAlignment(g195,g194)
    c: InternalAlignment(g196,g194)
    c: Block(g194)
    c: Block(g188)
    c: Block(g182)
    c: Block(g176)
    c: Coincident(g197,g194)
    c: Coincident(g197,g188)
    c: Horizontal(g197)
    c: Coincident(g198,g188)
    c: Coincident(g198,g19)
    c: Vertical(g198)
    c: Coincident(g199,g25)
    c: Coincident(g199,g182)
    c: Vertical(g199)
    c: Coincident(g200,g182)
    c: Coincident(g200,g176)
    c: Horizontal(g200)
    c: Coincident(g201,g176)
    c: Coincident(g201,g25)
    c: Coincident(g202,g19)
    c: Weight(g203) = 1
    c: Equal(g203,g204)
    c: Equal(g203,g205)
    c: InternalAlignment(g203,g206)
    c: InternalAlignment(g204,g206)
    c: InternalAlignment(g205,g206)
    c: InternalAlignment(g207,g206)
    c: InternalAlignment(g208,g206)
    c: Weight(g209) = 1
    c: Equal(g209,g210)
    c: Equal(g209,g211)
    c: InternalAlignment(g209,g212)
    c: InternalAlignment(g210,g212)
    c: InternalAlignment(g211,g212)
    c: InternalAlignment(g213,g212)
    c: InternalAlignment(g214,g212)
    c: Block(g212)
    c: Block(g206)
    c: Coincident(g215,g212)
    c: Coincident(g215,g43)
    c: Coincident(g216,g43)
    c: Coincident(g216,g206)
    c: Coincident(g217,g206)
    c: Coincident(g217,g212)
    c: Vertical(g217)
    c: Weight(g218) = 1
    c: Equal(g218,g219)
    c: Equal(g218,g220)
    c: InternalAlignment(g218,g221)
    c: InternalAlignment(g219,g221)
    c: InternalAlignment(g220,g221)
    c: InternalAlignment(g222,g221)
    c: InternalAlignment(g223,g221)
    c: Weight(g224) = 1
    c: Equal(g224,g225)
    c: Equal(g224,g226)
    c: InternalAlignment(g224,g227)
    c: InternalAlignment(g225,g227)
    c: InternalAlignment(g226,g227)
    c: InternalAlignment(g228,g227)
    c: InternalAlignment(g229,g227)
    c: Block(g227)
    c: Block(g221)
    c: Coincident(g230,g221)
    c: Coincident(g230,g49)
    c: Coincident(g231,g49)
    c: Coincident(g231,g227)
    c: Coincident(g232,g227)
    c: Coincident(g232,g221)
    c: Vertical(g232)
    c: Horizontal(g233)
    c: Block(g233)
    c: Vertical(g234)
    c: Block(g234)
    c: Block(g235)
    c: Weight(g236) = 1
    c: Equal(g236,g237)
    c: Equal(g236,g238)
    c: InternalAlignment(g236,g239)
    c: InternalAlignment(g237,g239)
    c: InternalAlignment(g238,g239)
    c: InternalAlignment(g240,g239)
    c: InternalAlignment(g241,g239)
    c: Weight(g242) = 1
    c: Equal(g242,g243)
    c: Equal(g242,g244)
    c: InternalAlignment(g242,g245)
    c: InternalAlignment(g243,g245)
    c: InternalAlignment(g244,g245)
    c: InternalAlignment(g246,g245)
    c: InternalAlignment(g247,g245)
    c: Weight(g248) = 1
    c: Equal(g248,g249)
    c: Equal(g248,g250)
    c: InternalAlignment(g248,g251)
    c: InternalAlignment(g249,g251)
    c: InternalAlignment(g250,g251)
    c: InternalAlignment(g252,g251)
    c: InternalAlignment(g253,g251)
    c: Weight(g254) = 1
    c: Equal(g254,g255)
    c: Equal(g254,g256)
    c: InternalAlignment(g254,g257)
    c: InternalAlignment(g255,g257)
    c: InternalAlignment(g256,g257)
    c: InternalAlignment(g258,g257)
    c: InternalAlignment(g259,g257)
    c: Block(g239)
    c: Block(g245)
    c: Block(g251)
    c: Block(g257)
    c: Coincident(g260,g245)
    c: Coincident(g260,g239)
    c: Horizontal(g260)
    c: Block(g202)
    c: Weight(g261) = 1
    c: Equal(g261,g262)
    c: Equal(g261,g263)
    c: InternalAlignment(g261,g264)
    c: InternalAlignment(g262,g264)
    c: InternalAlignment(g263,g264)
    c: InternalAlignment(g265,g264)
    c: InternalAlignment(g266,g264)
    c: Weight(g267) = 1
    c: Equal(g267,g268)
    c: Equal(g267,g269)
    c: InternalAlignment(g267,g270)
    c: InternalAlignment(g268,g270)
    c: InternalAlignment(g269,g270)
    c: InternalAlignment(g271,g270)
    c: InternalAlignment(g272,g270)
    c: Weight(g273) = 1
    c: Equal(g273,g274)
    c: Equal(g273,g275)
    c: InternalAlignment(g273,g276)
    c: InternalAlignment(g274,g276)
    c: InternalAlignment(g275,g276)
    c: InternalAlignment(g277,g276)
    c: InternalAlignment(g278,g276)
    c: Weight(g279) = 1
    c: Equal(g279,g280)
    c: Equal(g279,g281)
    c: InternalAlignment(g279,g282)
    c: InternalAlignment(g280,g282)
    c: InternalAlignment(g281,g282)
    c: InternalAlignment(g283,g282)
    c: InternalAlignment(g284,g282)
    c: Block(g264)
    c: Block(g270)
    c: Block(g276)
    c: Block(g282)
    c: Coincident(g285,g276)
    c: Coincident(g285,g282)
    c: Horizontal(g285)
    c: Coincident(g286,g282)
    c: Coincident(g286,g264)
    c: Vertical(g286)
    c: Coincident(g287,g264)
    c: Coincident(g287,g270)
    c: Coincident(g288,g270)
    c: Coincident(g288,g276)
    c: Vertical(g288)
    c: Weight(g289) = 1
    c: Equal(g289,g290)
    c: Equal(g289,g291)
    c: InternalAlignment(g289,g292)
    c: InternalAlignment(g290,g292)
    c: InternalAlignment(g291,g292)
    c: InternalAlignment(g293,g292)
    c: InternalAlignment(g294,g292)
    c: Weight(g295) = 1
    c: Equal(g295,g296)
    c: Equal(g295,g297)
    c: InternalAlignment(g295,g298)
    c: InternalAlignment(g296,g298)
    c: InternalAlignment(g297,g298)
    c: InternalAlignment(g299,g298)
    c: InternalAlignment(g300,g298)
    c: Weight(g301) = 1
    c: Equal(g301,g302)
    c: Equal(g301,g303)
    c: InternalAlignment(g301,g304)
    c: InternalAlignment(g302,g304)
    c: InternalAlignment(g303,g304)
    c: InternalAlignment(g305,g304)
    c: InternalAlignment(g306,g304)
    c: Block(g304)
    c: Block(g298)
    c: Block(g292)
    c: Coincident(g307,g298)
    c: Coincident(g307,g292)
    c: Coincident(g308,g292)
    c: Coincident(g308,g304)
    c: Vertical(g308)
    c: Coincident(g309,g304)
    c: Coincident(g309,g298)
    c: Horizontal(g309)
    c: Horizontal(g310)
    c: Horizontal(g313)
    c: Horizontal(g314)
    c: Vertical(g315)
    c: Vertical(g316)
    c: Horizontal(g317)
    c: Distance(g316) = 4
    c: Distance(g317) = 4
    c: Distance(g315) = 4
    c: Distance(g314) = 4
    c: Distance(g313) = 4
    c: Distance(g312) = 4
    c: Distance(g311) = 4
    c: Distance(g310) = 4
FEATURE [Sketcher::SketchObject] Sketch001
  FullyConstrained = true
  MapMode = 4
  Placement = pos=(0,0,0) rot=(0.57735,0.57735,0.57735;2.0944rad)
  Support = -> [Sketch]
  sketch-geometry (46):
    g0: BSplineCurve PolesCount=3 KnotsCount=2 Degree=2 IsPeriodic=0
    g1: ArcOfCircle CenterX=73.1223 CenterY=-32.291 CenterZ=0 NormalX=0 NormalY=0 NormalZ=1 AngleXU=0 Radius=13 StartAngle=5.92268 EndAngle=9.06428
    g2: ArcOfCircle CenterX=66.7816 CenterY=-49.1439 CenterZ=0 NormalX=0 NormalY=0 NormalZ=1 AngleXU=0 Radius=13 StartAngle=2.78068 EndAngle=5.92131
    g3: ArcOfCircle CenterX=55.9263 CenterY=-78.1807 CenterZ=0 NormalX=0 NormalY=0 NormalZ=1 AngleXU=0 Radius=13 StartAngle=5.92268 EndAngle=9.06428
    g4: ArcOfCircle CenterX=49.5884 CenterY=-95.0342 CenterZ=0 NormalX=0 NormalY=0 NormalZ=1 AngleXU=0 Radius=13 StartAngle=2.78068 EndAngle=5.92131
    g5: ArcOfCircle CenterX=38.7206 CenterY=-124.067 CenterZ=0 NormalX=0 NormalY=0 NormalZ=1 AngleXU=0 Radius=13 StartAngle=5.92268 EndAngle=9.06428
    g6: ArcOfCircle CenterX=32.3875 CenterY=-140.92 CenterZ=0 NormalX=0 NormalY=0 NormalZ=1 AngleXU=0 Radius=13 StartAngle=2.78068 EndAngle=5.92131
    g7: ArcOfCircle CenterX=21.4715 CenterY=-169.934 CenterZ=0 NormalX=0 NormalY=0 NormalZ=1 AngleXU=0 Radius=13 StartAngle=5.92268 EndAngle=9.06428
    g8: ArcOfCircle CenterX=15.1336 CenterY=-186.787 CenterZ=0 NormalX=0 NormalY=0 NormalZ=1 AngleXU=0 Radius=13 StartAngle=2.78068 EndAngle=5.92131
    g9-g12: Circle x4 (B-spline internal-alignment scaffolding for g13; pole/knot coordinates omitted)
    g13: BSplineCurve PolesCount=4 KnotsCount=2 Degree=3 IsPeriodic=0
    g14: GeomPoint X=28.8094 Y=-19.0875 Z=0
    g15: GeomPoint X=47.0443 Y=-50.4712 Z=0
    g16: Circle CenterX=53.5586 CenterY=-23.2695 CenterZ=0 NormalX=0 NormalY=0 NormalZ=1 AngleXU=0 Radius=3.24518
    g17: Circle CenterX=-195.441 CenterY=-127.082 CenterZ=0 NormalX=0 NormalY=0 NormalZ=1 AngleXU=0 Radius=1
    g18: Circle CenterX=-8.24091 CenterY=-197.481 CenterZ=0 NormalX=0 NormalY=0 NormalZ=1 AngleXU=0 Radius=1
    g19: Circle CenterX=12.8789 CenterY=-141.321 CenterZ=0 NormalX=0 NormalY=0 NormalZ=1 AngleXU=0 Radius=1
    g20: BSplineCurve PolesCount=3 KnotsCount=2 Degree=2 IsPeriodic=0
    g21: GeomPoint X=-195.441 Y=-127.082 Z=0
    g22: GeomPoint X=12.8789 Y=-141.321 Z=0
    g23: Circle CenterX=-12.8016 CenterY=-179.036 CenterZ=0 NormalX=0 NormalY=0 NormalZ=1 AngleXU=0 Radius=10.5072
    g24: Circle CenterX=0.933922 CenterY=-166.43 CenterZ=0 NormalX=0 NormalY=0 NormalZ=1 AngleXU=0 Radius=3.26661
    g25: Circle CenterX=-33.5518 CenterY=-176.44 CenterZ=0 NormalX=0 NormalY=0 NormalZ=1 AngleXU=0 Radius=5.64388
    g26: Circle CenterX=-47.2366 CenterY=-173.859 CenterZ=0 NormalX=0 NormalY=0 NormalZ=1 AngleXU=0 Radius=3.01653
    g27: Circle CenterX=-56.2595 CenterY=-171.456 CenterZ=0 NormalX=0 NormalY=0 NormalZ=1 AngleXU=0 Radius=2.12826
    g28: ArcOfCircle CenterX=51.2151 CenterY=-198.473 CenterZ=0 NormalX=0 NormalY=0 NormalZ=1 AngleXU=0 Radius=20 StartAngle=2.78189 EndAngle=4.35269
    g29: LineSegment StartX=32.4951 StartY=-191.433 StartZ=0 EndX=94.6578 EndY=-26.1352 EndZ=0
    g30: LineSegment StartX=43.1192 StartY=-220.001 StartZ=0 EndX=-196.497 EndY=-129.89 EndZ=0
    g31: LineSegment StartX=43.1192 StartY=-220.001 StartZ=0 EndX=44.1752 EndY=-217.193 EndZ=0
    g32: LineSegment StartX=117.223 StartY=-19.0875 StartZ=0 EndX=117.223 EndY=-16.0875 EndZ=0
    g33: LineSegment StartX=117.223 StartY=-16.0875 StartZ=0 EndX=17.2232 EndY=-16.0875 EndZ=0
    g34: LineSegment StartX=17.2232 StartY=-16.0875 StartZ=0 EndX=17.2232 EndY=-19.0875 EndZ=0
    g35: LineSegment StartX=28.8094 StartY=-19.0875 StartZ=0 EndX=17.2232 EndY=-19.0875 EndZ=0
    g36: LineSegment StartX=47.0443 StartY=-50.4712 StartZ=0 EndX=12.8789 EndY=-141.321 EndZ=0
    g37: LineSegment StartX=-195.441 StartY=-127.082 StartZ=0 EndX=-196.497 EndY=-129.89 EndZ=0
    g38: LineSegment StartX=85.2866 StartY=-36.8766 StartZ=0 EndX=78.9396 EndY=-53.7463 EndZ=0
    g39: LineSegment StartX=60.9579 StartY=-27.7053 StartZ=0 EndX=54.6191 EndY=-44.5532 EndZ=0
    g40: LineSegment StartX=68.0907 StartY=-82.7664 StartZ=0 EndX=61.7465 EndY=-99.6365 EndZ=0
    g41: LineSegment StartX=43.7619 StartY=-73.595 StartZ=0 EndX=37.426 EndY=-90.4435 EndZ=0
    g42: LineSegment StartX=50.885 StartY=-128.652 StartZ=0 EndX=44.5456 EndY=-145.522 EndZ=0
    g43: LineSegment StartX=26.5562 StartY=-119.481 StartZ=0 EndX=20.2251 EndY=-136.329 EndZ=0
    g44: LineSegment StartX=9.3071 StartY=-165.349 StartZ=0 EndX=2.97115 EndY=-182.197 EndZ=0
    g45: LineSegment StartX=33.6358 StartY=-174.52 StartZ=0 EndX=27.2917 EndY=-191.39 EndZ=0
  constraints (71):
    c: Block(g0)
    c: Block(g1)
    c: Block(g2)
    c: Block(g4)
    c: Block(g3)
    c: Block(g6)
    c: Block(g5)
    c: Block(g8)
    c: Block(g7)
    c: Weight(g9) = 1
    c: Equal(g9,g10)
    c: Equal(g9,g11)
    c: Equal(g9,g12)
    c: InternalAlignment(g9-g12 -> g13) x4
    c: InternalAlignment(g14,g13)
    c: InternalAlignment(g15,g13)
    c: Block(g16)
    c: Weight(g17) = 1
    c: Equal(g17,g18)
    c: Equal(g17,g19)
    c: InternalAlignment(g17,g20)
    c: InternalAlignment(g18,g20)
    c: InternalAlignment(g19,g20)
    c: InternalAlignment(g21,g20)
    c: InternalAlignment(g22,g20)
    c: Block(g20)
    c: Block(g23)
    c: Block(g24)
    c: Block(g25)
    c: Block(g26)
    c: Block(g27)
    c: Block(g28)
    c: Coincident(g29,g28)
    c: Coincident(g29,g0)
    c: Block(g13)
    c: Coincident(g31,g30)
    c: Coincident(g31,g28)
    c: Block(g31)
    c: Coincident(g32,g0)
    c: Vertical(g32)
    c: Coincident(g33,g32)
    c: Horizontal(g33)
    c: Coincident(g34,g33)
    c: Vertical(g34)
    c: Block(g33)
    c: Coincident(g35,g13)
    c: Coincident(g35,g34)
    c: Horizontal(g35)
    c: Coincident(g36,g13)
    c: Coincident(g36,g20)
    c: Coincident(g37,g20)
    c: Coincident(g37,g30)
    c: Block(g30)
    c: Coincident(g38,g1)
    c: Coincident(g38,g2)
    c: Coincident(g39,g1)
    c: Coincident(g39,g2)
    c: Coincident(g40,g3)
    c: Coincident(g40,g4)
    c: Coincident(g41,g3)
    c: Coincident(g41,g4)
    c: Coincident(g42,g5)
    c: Coincident(g42,g6)
    c: Coincident(g43,g5)
    c: Coincident(g43,g6)
    c: Coincident(g44,g7)
    c: Coincident(g44,g8)
    c: Coincident(g45,g7)
    c: Coincident(g45,g8)
    c: Distance(g30) = 256
    c: Distance(g33) = 100
FEATURE [Part::Extrusion] Extrude002
  Base = -> Sketch001
  Dir = (1,0,0)
  DirMode = 2
  FaceMakerClass = Part::FaceMakerBullseye
  LengthFwd = 8
  LengthRev = 0
  Solid = true
  Symmetric = false
FEATURE [Sketcher::SketchObject] Sketch002
  FullyConstrained = true
  sketch-geometry (20):
    g0: LineSegment StartX=-2.77179 StartY=-200.304 StartZ=0 EndX=5.22821 EndY=-200.304 EndZ=0
    g1: LineSegment StartX=5.22821 StartY=-200.304 StartZ=0 EndX=5.22821 EndY=-197.304 EndZ=0
    g2: LineSegment StartX=-2.77179 StartY=-200.304 StartZ=0 EndX=-2.77179 EndY=-197.304 EndZ=0
    g3: LineSegment StartX=5.22821 StartY=-197.304 StartZ=0 EndX=8.22821 EndY=-197.304 EndZ=0
    g4: LineSegment StartX=-2.77179 StartY=-197.304 StartZ=0 EndX=-5.77179 EndY=-197.304 EndZ=0
    g5: LineSegment StartX=19.2282 StartY=-203.304 StartZ=0 EndX=19.2282 EndY=-206.304 EndZ=0
    g6: LineSegment StartX=-16.7718 StartY=-203.304 StartZ=0 EndX=-16.7718 EndY=-206.304 EndZ=0
    g7: LineSegment StartX=-16.7718 StartY=-206.304 StartZ=0 EndX=19.2282 EndY=-206.304 EndZ=0
    g8: Circle CenterX=-16.7718 CenterY=-203.304 CenterZ=0 NormalX=0 NormalY=0 NormalZ=1 AngleXU=0 Radius=1
    g9: Circle CenterX=-5.77179 CenterY=-203.304 CenterZ=0 NormalX=0 NormalY=0 NormalZ=1 AngleXU=0 Radius=1
    g10: Circle CenterX=-5.77179 CenterY=-197.304 CenterZ=0 NormalX=0 NormalY=0 NormalZ=1 AngleXU=0 Radius=1
    g11: BSplineCurve PolesCount=3 KnotsCount=2 Degree=2 IsPeriodic=0
    g12: GeomPoint X=-16.7718 Y=-203.304 Z=0
    g13: GeomPoint X=-5.77179 Y=-197.304 Z=0
    g14: Circle CenterX=19.2282 CenterY=-203.304 CenterZ=0 NormalX=0 NormalY=0 NormalZ=1 AngleXU=0 Radius=1
    g15: Circle CenterX=8.22821 CenterY=-203.304 CenterZ=0 NormalX=0 NormalY=0 NormalZ=1 AngleXU=0 Radius=1
    g16: Circle CenterX=8.22821 CenterY=-197.304 CenterZ=0 NormalX=0 NormalY=0 NormalZ=1 AngleXU=0 Radius=1
    g17: BSplineCurve PolesCount=3 KnotsCount=2 Degree=2 IsPeriodic=0
    g18: GeomPoint X=19.2282 Y=-203.304 Z=0
    g19: GeomPoint X=8.22821 Y=-197.304 Z=0
  constraints (41):
    c: Horizontal(g0)
    c: Distance(g0) = 8
    c: Coincident(g1,g0)
    c: Vertical(g1)
    c: Distance(g1) = 3
    c: Coincident(g2,g0)
    c: Vertical(g2)
    c: Distance(g2) = 3
    c: Coincident(g3,g1)
    c: Horizontal(g3)
    c: Distance(g3) = 3
    c: Coincident(g4,g2)
    c: Horizontal(g4)
    c: Distance(g4) = 3
    c: Vertical(g5)
    c: Vertical(g6)
    c: Coincident(g7,g6)
    c: Coincident(g7,g5)
    c: Weight(g8) = 1
    c: Equal(g8,g9)
    c: Equal(g8,g10)
    c: Coincident(g11,g4)
    c: InternalAlignment(g8,g11)
    c: InternalAlignment(g9,g11)
    c: InternalAlignment(g10,g11)
    c: InternalAlignment(g12,g11)
    c: InternalAlignment(g13,g11)
    c: Coincident(g17,g5)
    c: Weight(g14) = 1
    c: Equal(g14,g15)
    c: Equal(g14,g16)
    c: Coincident(g17,g3)
    c: InternalAlignment(g14,g17)
    c: InternalAlignment(g15,g17)
    c: InternalAlignment(g16,g17)
    c: InternalAlignment(g18,g17)
    c: InternalAlignment(g19,g17)
    c: Block(g7)
    c: Block(g17)
    c: Block(g11)
    c: Block(g6)
FEATURE [Part::Extrusion] Extrude003
  Base = -> Sketch002
  Dir = (0,0,1)
  DirMode = 2
  FaceMakerClass = Part::FaceMakerBullseye
  LengthFwd = 260
  LengthRev = 0
  Solid = true
  Symmetric = false
FEATURE [Part::Extrusion] Extrude
  Base = -> Sketch
  Dir = (0,0,1)
  DirMode = 2
  FaceMakerClass = Part::FaceMakerBullseye
  LengthFwd = 14
  LengthRev = 0
  Solid = true
  Symmetric = false
